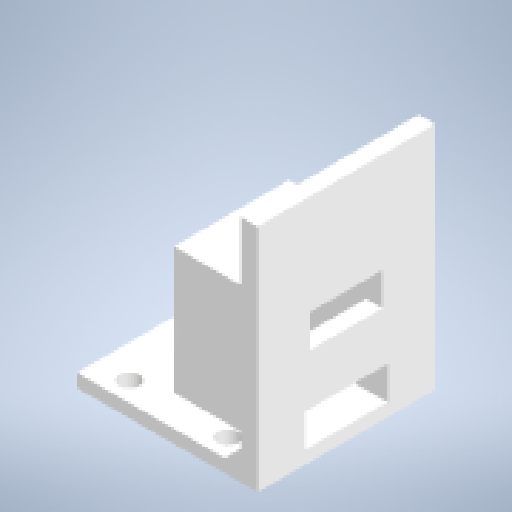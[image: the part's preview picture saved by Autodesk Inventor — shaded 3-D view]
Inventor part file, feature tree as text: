
AUTODESK INVENTOR PART (.ipt)
format: ipt  version: 2025 (Build 290162000, 162)  size: 245,248 bytes
history: native  units: mm
features: extrude x9, sketch x4, other x1, projected_geometry x1
ambient origin geometry x8: Origin, YZ Plane, XZ Plane, XY Plane, X Axis, Y Axis, Z Axis, Center Point
bodies: Body1 (feature_tree)
feature tree (15):
  other  "Bryła1"
  sketch  "Szkic1"
  extrude  "Wyciągnięcie proste1"  Depth=50.0mm
  extrude  "Wyciągnięcie proste2"  Depth=10.0mm
  extrude  "Wyciągnięcie proste3"  Depth=6.0mm
  extrude  "Wyciągnięcie proste4"  Depth=6.0mm
  extrude  "Wyciągnięcie proste5"  Depth=5.0mm
  extrude  "Wyciągnięcie proste6"  Depth=54.0mm
  extrude  "Wyciągnięcie proste7"  Depth=54.0mm
  extrude  "Wyciągnięcie proste8"  Depth=4.0mm TaperAngle=0.0deg
  extrude  "Wyciągnięcie proste9"  Depth=70.0mm TaperAngle=0.0deg
  sketch  "Szkic3"
  sketch  "Szkic9"
  sketch  "Szkic10"
  projected_geometry  "Pętla rzutowana1"
